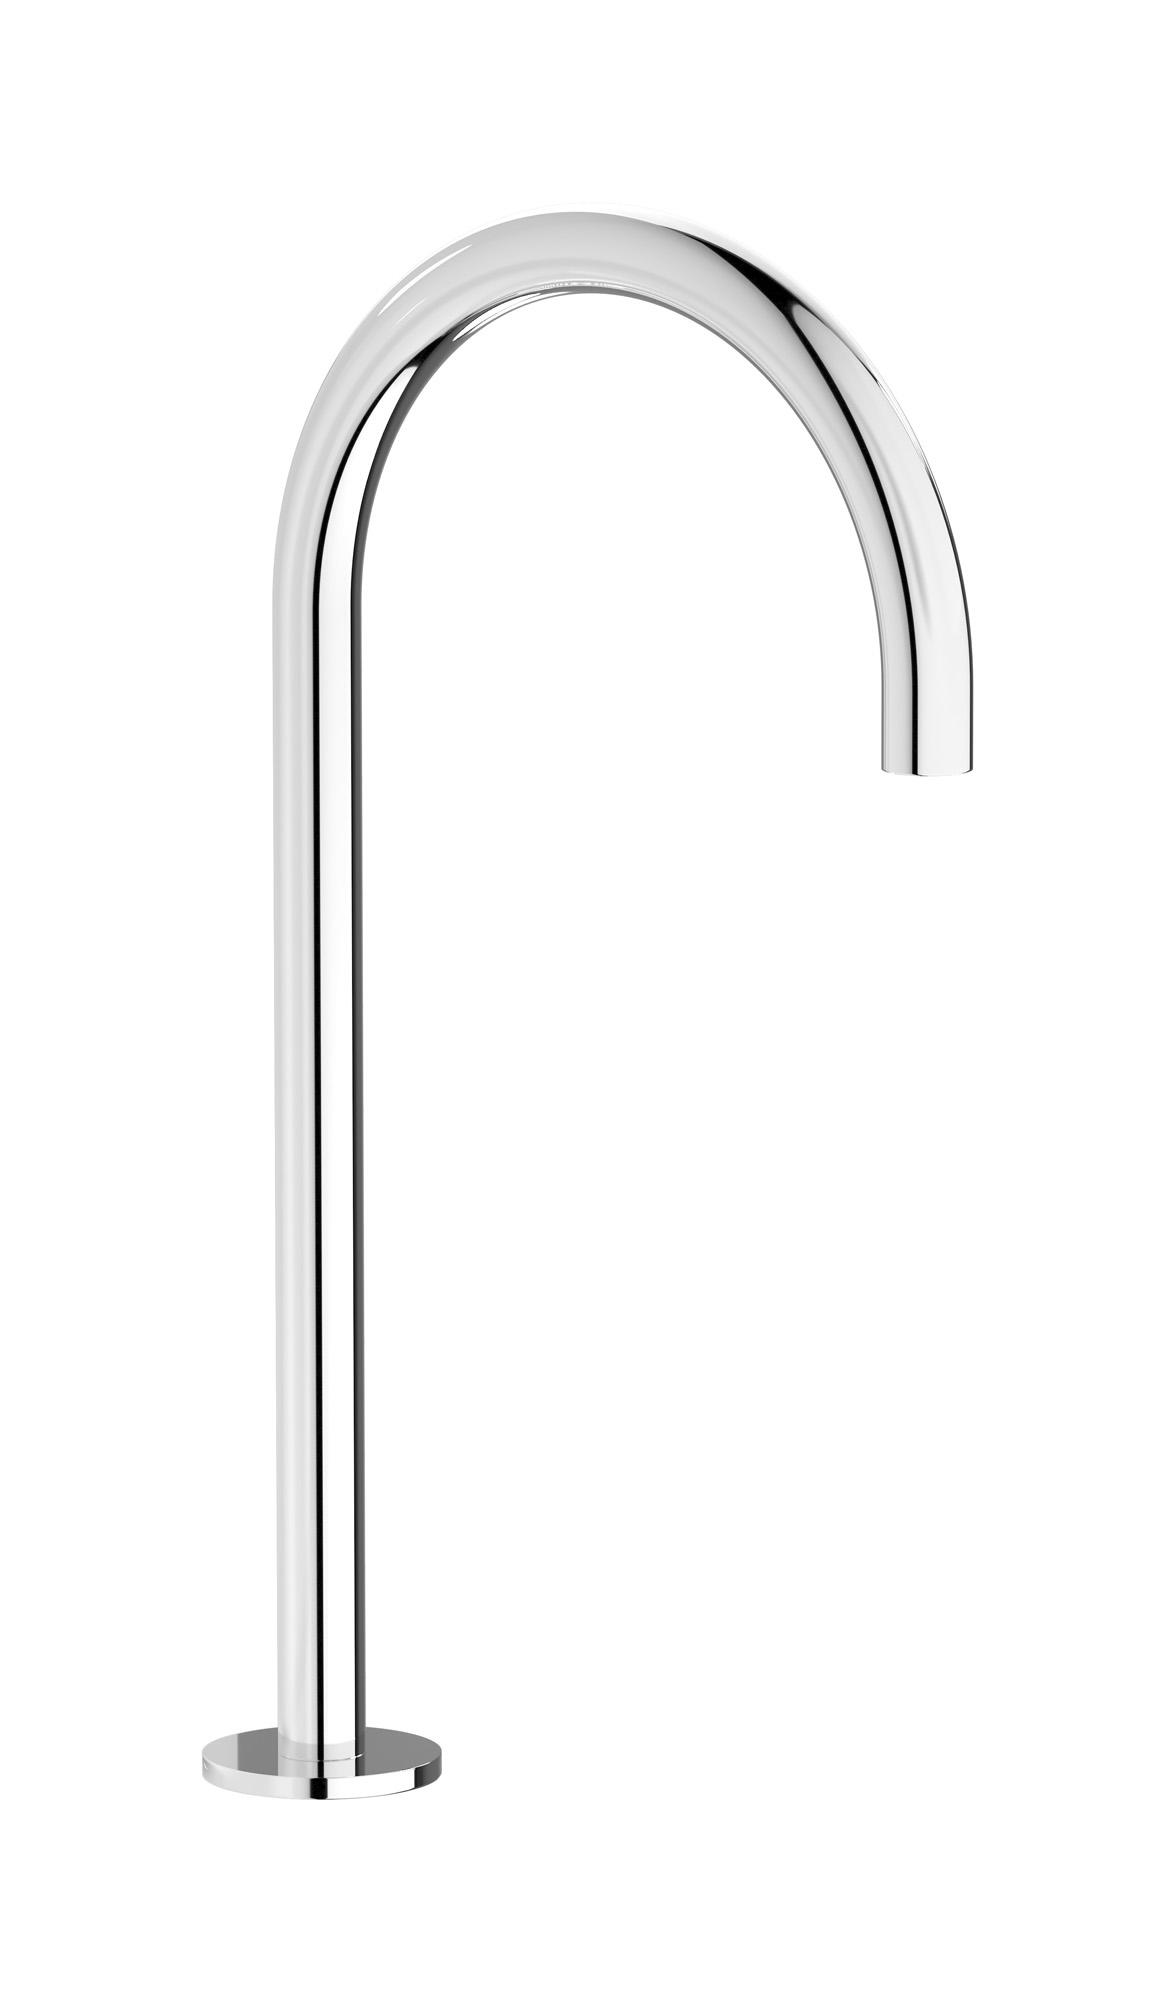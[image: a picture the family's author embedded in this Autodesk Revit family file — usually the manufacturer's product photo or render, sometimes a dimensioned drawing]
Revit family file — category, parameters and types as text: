
# Revit family: RX395
name_source: partatom
category: Apparecchi idraulici
units: mm (PartAtom-declared; Revit-internal decimal feet)

## family parameters
Basato su piano di lavoro = No
Condiviso = No
Mantieni orientamento annotazione = No
Numero OmniClass = 23.45.55.17
Punto di calcolo locali = No
Quota connettore circolare = Usa diametro
Sempre verticale = Sì
Taglio con vuoti quando caricato = No
Tipo di parte = Normale
Titolo OmniClass = Mixing Faucets

## types (12) — shared parameters
Commenti sul tipo = Tall deck mounted spout complete with drain
Connessione CW = No
Connessione HW = No
Connessione di scarico = No
Connessione di ventilazione = No
Descrizione = Tall deck mounted spout complete with drain
Produttore = IB Rubinetterie S.p.A.
URL = https://www.weareib.it
Water inlet = 10 mm  [stored 0.0328084 ft]
zero-valued in all types: Prospetto di default

## per-type parameters (varying)
| type | Finishes surface | Immagine tipo | Modello |
| Chrome | IB_Chrome | RX395CC.jpg | RX395CC |
| Black Chrome | IB_Black chrome | RX395CF.jpg | RX395CF |
| Brushed Black Chrome | IB_Brushed black chrome | RX395CS.jpg | RX395CS |
| Pale Gold | IB_Pale gold | RX395II.jpg | RX395II |
| Brushed Pale Gold | IB_brushed pale gold | RX395IS.jpg | RX395IS |
| Matt Black | IB_matt black | RX395NP.jpg | RX395NP |
| Natural Brass | IB_Brass | RX395ON.jpg | RX395ON |
| Gold | IB_gold | RX395OO.jpg | RX395OO |
| Brushed Gold | IB_brushed gold | RX395OS.jpg | RX395OS |
| Rose Gold | IB_Rose gold | RX395RS.jpg | RX395RS |
| Brushed Rose Gold | IB_Brushed rose gold | RX395SR.jpg | RX395SR |
| Brushed Nickel | IB_Brushed nickel | RX395SS.jpg | RX395SS |

note: [stored X ft] marks values corroborated as IEEE doubles in the binary element streams (Revit-internal decimal feet)
